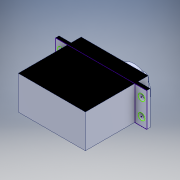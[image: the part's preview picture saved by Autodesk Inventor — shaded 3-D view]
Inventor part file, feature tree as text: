
AUTODESK INVENTOR PART (.ipt)
format: ipt  version: 2018 (Build 220112000, 112)  size: 155,136 bytes
history: native  units: mm
features: sketch x1, other x1
ambient origin geometry x8: Origin, YZ Plane, XZ Plane, XY Plane, X Axis, Y Axis, Z Axis, Center Point
bodies: Solid1 (feature_tree)
feature tree (2):
  sketch  "Sketch7"
  other  "Saliente-Extruir6"
